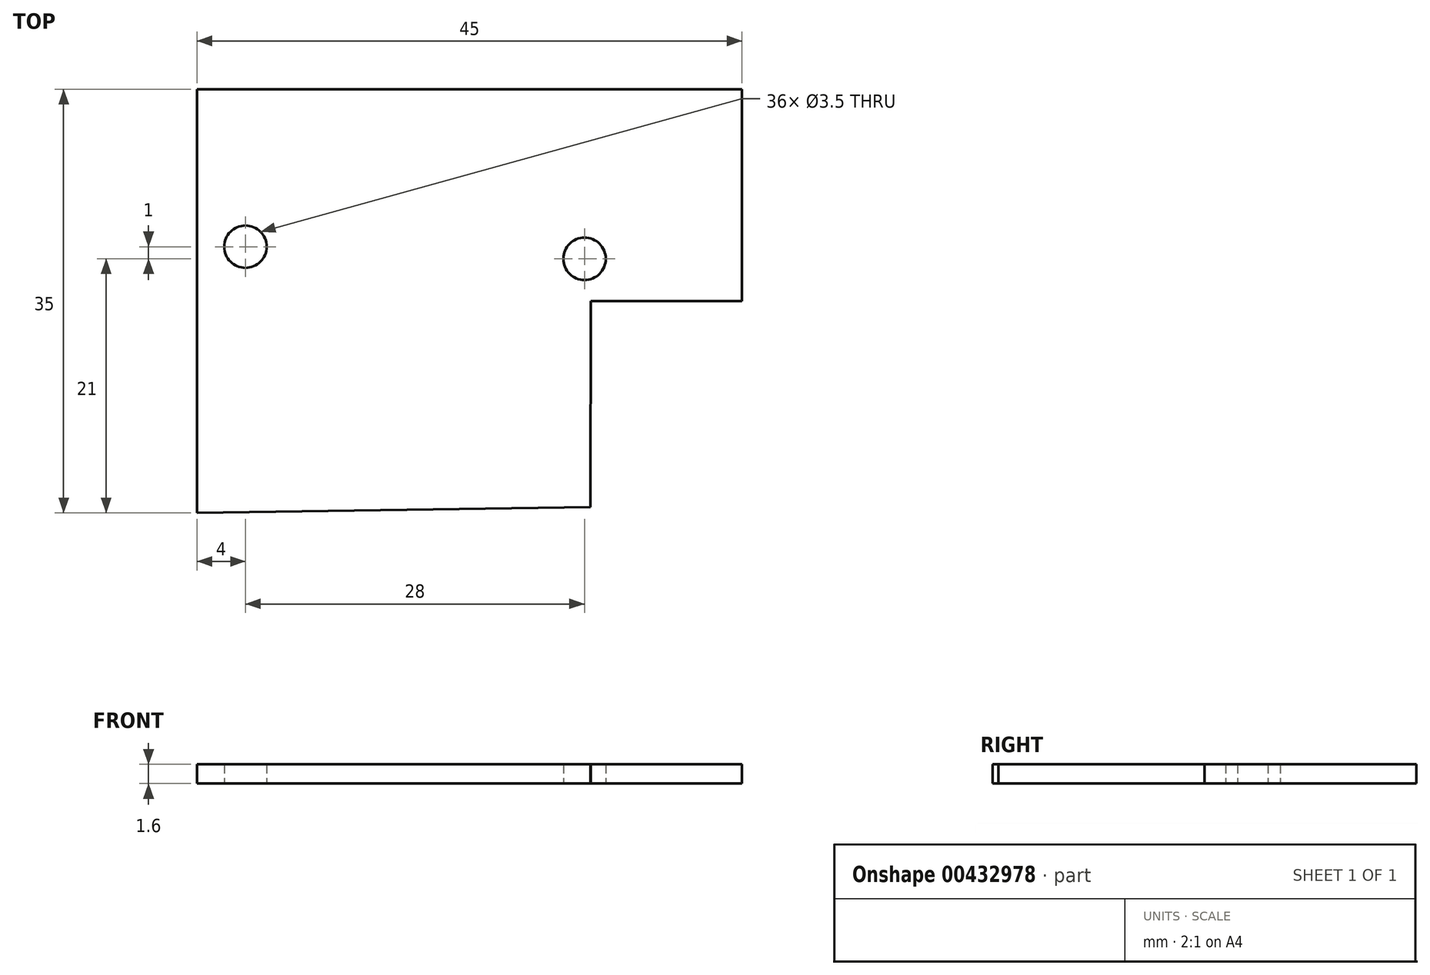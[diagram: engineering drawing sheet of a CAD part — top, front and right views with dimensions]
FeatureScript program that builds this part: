
annotation { "Feature Type Name" : "Feature", "Feature Type Description" : "" }
export const myFeature = defineFeature(function(context is Context, id is Id, definition is map)
    precondition{}
    {
        {
            var Q0;
            Q0=qCreatedBy(makeId("Top.planeOp"),FACE);
            var sketch = newSketch(context, id + "F0", { "sketchPlane" : qUnion([Q0])});
            skLineSegment(sketch, "E0", {"start": v(0, 0) * mm, "end": v(45, 0) * mm});
            skLineSegment(sketch, "E1", {"start": v(45, 0) * mm, "end": v(45, -17.5) * mm});
            skLineSegment(sketch, "E2", {"start": v(45, -17.5) * mm, "end": v(32.5, -17.5) * mm});
            skLineSegment(sketch, "E3", {"start": v(32.5, -17.5) * mm, "end": v(32.5, -34.5) * mm});
            skLineSegment(sketch, "E4", {"start": v(32.5, -34.5) * mm, "end": v(0, -35) * mm});
            skLineSegment(sketch, "E5", {"start": v(0, -35) * mm, "end": v(0, 0) * mm});
            skPoint(sketch, "E6", {"position": v(4, -13) * mm});
            skPoint(sketch, "E7", {"position": v(32, -14) * mm});
            skCircle(sketch, "E8", {"center": v(4, -13) * mm, "radius": 1.75 * mm});
            skCircle(sketch, "E9", {"center": v(32, -14) * mm, "radius": 1.75 * mm});
            skSolve(sketch);
        }
        {
            var Q0;
            Q0 = qSketchRegion(id + "F0", true);
            extrude(context, id + "F1", {"entities" : qUnion([Q0]), "depth" : 1.6 * mm});
        }
    });
